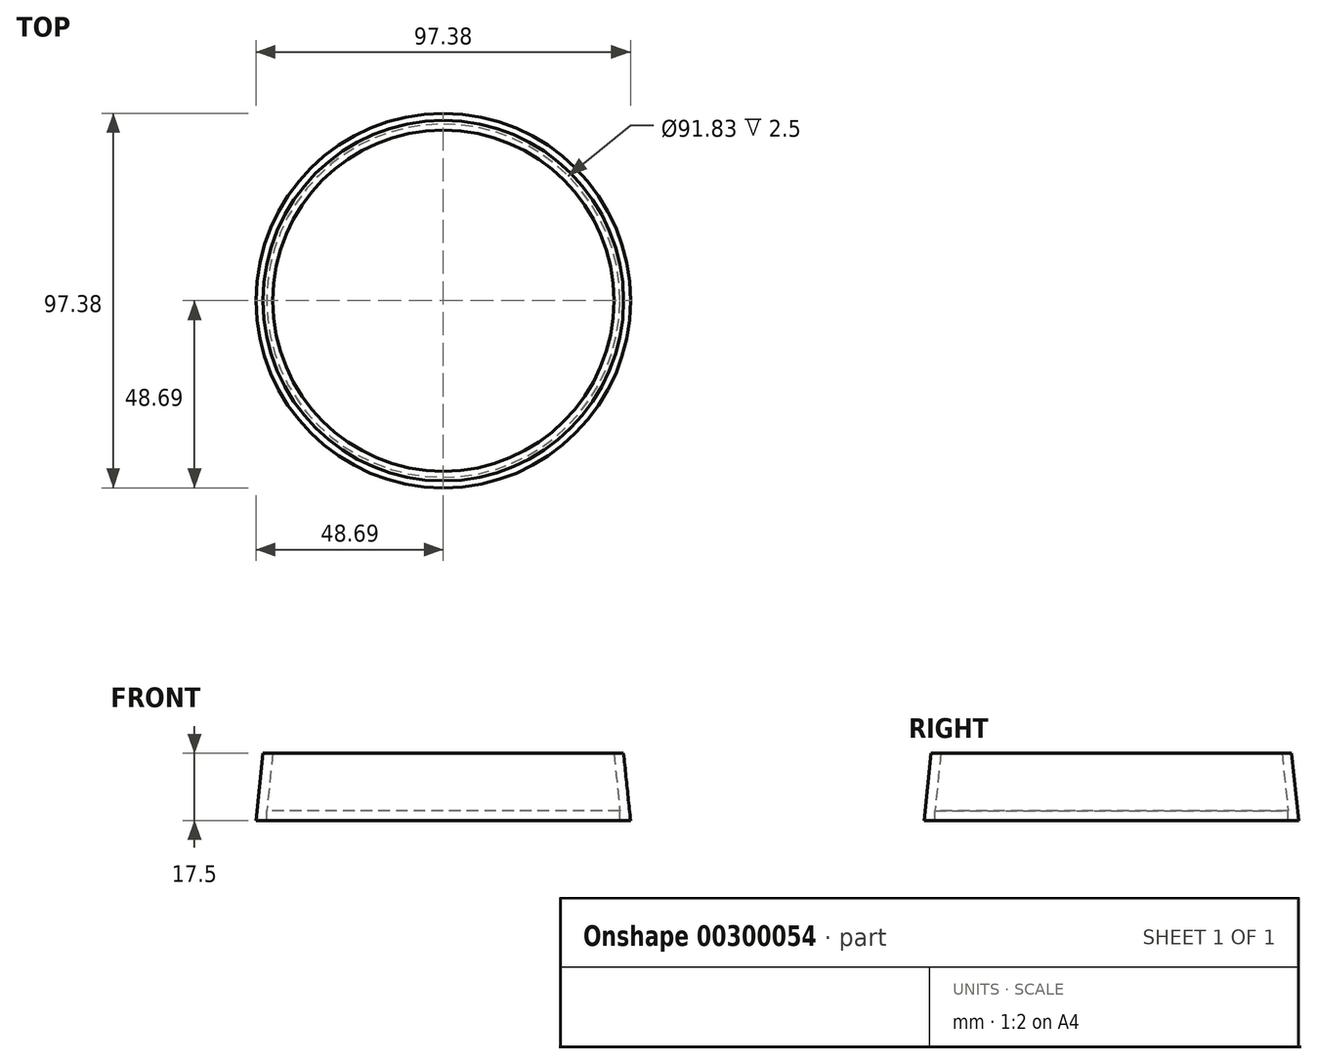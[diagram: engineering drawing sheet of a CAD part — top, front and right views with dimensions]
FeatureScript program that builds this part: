
annotation { "Feature Type Name" : "Feature", "Feature Type Description" : "" }
export const myFeature = defineFeature(function(context is Context, id is Id, definition is map)
    precondition{}
    {
        {
            assignVariable(context, id + "F0", {"name" : "bucket_t", "anyValue" : 0.75});
        }
        {
            assignVariable(context, id + "F1", {"name" : "bucket_top_d", "anyValue" : 117 - (getVariable(context, 'bucket_t') * 2)});
        }
        {
            assignVariable(context, id + "F2", {"name" : "bucket_bot_d", "anyValue" : 88 - (getVariable(context, 'bucket_t') * 2)});
        }
        {
            assignVariable(context, id + "F3", {"name" : "bucket_h", "anyValue" : 140});
        }
        {
            assignVariable(context, id + "F4", {"name" : "bucket_angle", "anyValue" : atan(((getVariable(context, 'bucket_top_d') - getVariable(context, 'bucket_bot_d')) / 2) / getVariable(context, 'bucket_h'))});
        }
        {
            assignVariable(context, id + "F5", {"name" : "screen_h", "anyValue" : 2.5});
        }
        {
            assignVariable(context, id + "F6", {"name" : "rim_h", "anyValue" : 15});
        }
        {
            assignVariable(context, id + "F7", {"name" : "spacer_h", "anyValue" : getVariable(context, 'screen_h') + getVariable(context, 'rim_h')});
        }
        {
            var Q0;
            Q0=qCreatedBy(makeId("Top.planeOp"),FACE);
            var sketch = newSketch(context, id + "F8", { "sketchPlane" : qUnion([Q0])});
            skCircle(sketch, "E0", {"center": v(0, 0) * mm, "radius": 48.69 * mm});
            skSolve(sketch);
        }
        {
            var Q0;
            Q0=makeQuery(id+"F8.imprint","IMPRINT",FACE,{"disambiguationData":[TD([[makeQuery(id+"F8.imprint","IMPRINT",EDGE,{"derivedFrom":sQuery(id+"F8.wireOp",EDGE,"E0")}),1.0]])]});
            extrude(context, id + "F9", {"entities" : qUnion([Q0]), "depth" : (getVariable(context, 'spacer_h')) * mm, "hasDraft" : true, "draftAngle" : getVariable(context, 'bucket_angle'), "draftPullDirection" : true});
        }
        {
            var Q0;
            Q0=makeQuery(id+"F9.opExtrude","CAP_FACE",FACE,{"disambiguationData":[OSD([sQuery(id+"F8.wireOp",EDGE,"E0")])],"isStart":false});
            shell(context, id + "F10", {"entities" : qUnion([Q0]), "thickness" : (getVariable(context, 'screen_h')) * mm});
        }
        {
            var Q0;
            {var subQ0=sQuery(id+"F8.wireOp",EDGE,"E0");Q0=makeQuery(id+"F10.opShell","OFFSET_FACE",FACE,{"disambiguationData":[OSD([subQ0]),TDD([makeQuery(id+"F9.opExtrude","CAP_FACE",FACE,{"disambiguationData":[OSD([subQ0])],"isStart":true})])]});}
            var sketch = newSketch(context, id + "F11", { "sketchPlane" : qUnion([Q0])});
            skCircle(sketch, "E1.0.0", {"center": v(0, 0) * mm, "radius": 45.92 * mm});
            skSolve(sketch);
        }
        {
            var Q0;
            Q0 = qSketchRegion(id + "F11", true);
            var Q1;
            Q1=makeQuery(id+"F9.opExtrude","CAP_FACE",FACE,{"disambiguationData":[OSD([sQuery(id+"F8.wireOp",EDGE,"E0")])],"isStart":true});
            extrude(context, id + "F12", {"entities" : qUnion([Q0]), "operationType" : NewBodyOperationType.REMOVE, "endBound" : BoundingType.UP_TO_SURFACE, "oppositeDirection" : true, "endBoundEntityFace" : qUnion([Q1]), "depth" : 25 * mm});
        }
        {
            var Q0;
            Q0 = qSketchRegion(id + "F11", true);
            var Q1;
            Q1=makeQuery(id+"F9.opExtrude","CAP_FACE",FACE,{"disambiguationData":[OSD([sQuery(id+"F8.wireOp",EDGE,"E0")])],"isStart":true});
            extrude(context, id + "F13", {"entities" : qUnion([Q0]), "endBound" : BoundingType.UP_TO_SURFACE, "oppositeDirection" : true, "endBoundEntityFace" : qUnion([Q1]), "depth" : 25 * mm});
        }
    });
